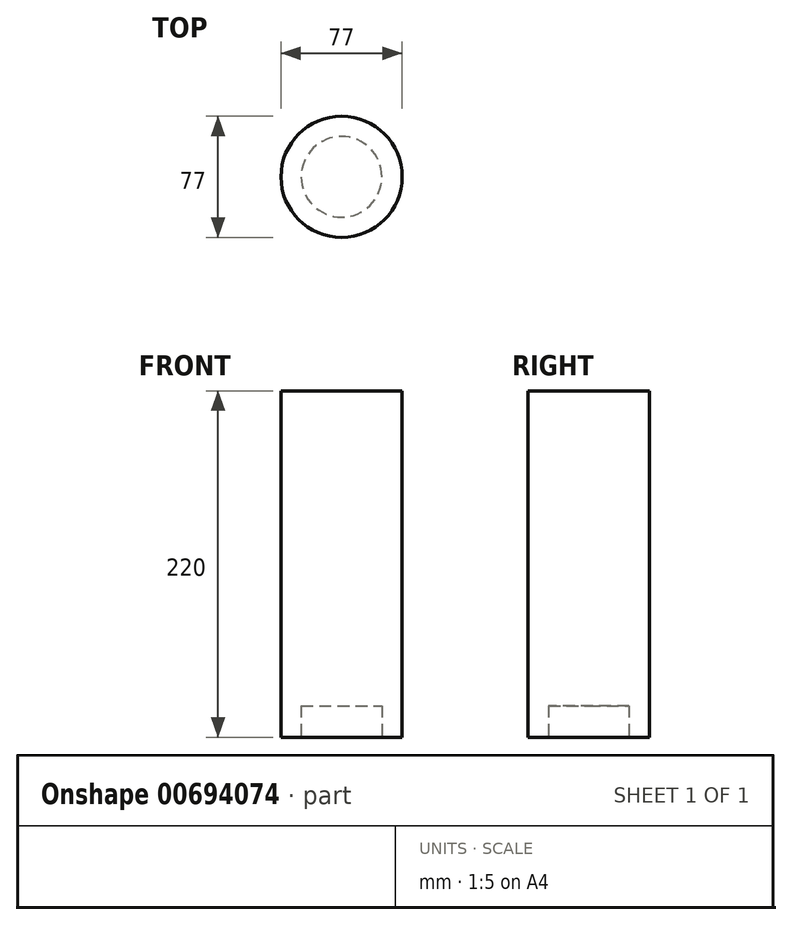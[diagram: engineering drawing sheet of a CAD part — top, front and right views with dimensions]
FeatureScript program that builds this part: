
annotation { "Feature Type Name" : "Feature", "Feature Type Description" : "" }
export const myFeature = defineFeature(function(context is Context, id is Id, definition is map)
    precondition{}
    {
        {
            var Q0;
            Q0=qCreatedBy(makeId("Front.planeOp"),FACE);
            var sketch = newSketch(context, id + "F0", { "sketchPlane" : qUnion([Q0])});
            skLineSegment(sketch, "E0", {"start": v(0, 0) * mm, "end": v(0, 86.33) * mm});
            skLineSegment(sketch, "E1", {"start": v(0, 0) * mm, "end": v(38.5, 0) * mm});
            skLineSegment(sketch, "E2", {"start": v(38.5, 0) * mm, "end": v(38.5, 220) * mm});
            skLineSegment(sketch, "E3", {"start": v(38.5, 220) * mm, "end": v(0, 220) * mm});
            skLineSegment(sketch, "E4", {"start": v(0, 86.33) * mm, "end": v(0, 220) * mm});
            skLineSegment(sketch, "E5.bottom", {"start": v(0, 220) * mm, "end": v(22.5, 220) * mm});
            skLineSegment(sketch, "E5.top", {"start": v(0, 340) * mm, "end": v(22.5, 340) * mm});
            skLineSegment(sketch, "E5.left", {"start": v(0, 220) * mm, "end": v(0, 340) * mm});
            skLineSegment(sketch, "E5.right", {"start": v(22.5, 220) * mm, "end": v(22.5, 340) * mm});
            skLineSegment(sketch, "E6.top", {"start": v(0, 280) * mm, "end": v(22.5, 280) * mm});
            skLineSegment(sketch, "E6.left", {"start": v(0, 220) * mm, "end": v(0, 280) * mm});
            skLineSegment(sketch, "E6.right", {"start": v(22.5, 220) * mm, "end": v(22.5, 280) * mm});
            skLineSegment(sketch, "E7.bottom", {"start": v(0, 280) * mm, "end": v(20.06, 280) * mm});
            skLineSegment(sketch, "E7.top", {"start": v(0, 340) * mm, "end": v(20.06, 340) * mm});
            skLineSegment(sketch, "E7.left", {"start": v(0, 280) * mm, "end": v(0, 340) * mm});
            skLineSegment(sketch, "E7.right", {"start": v(20.06, 280) * mm, "end": v(20.06, 340) * mm});
            skSolve(sketch);
        }
        {
            var Q0;
            Q0=makeQuery(id+"F0.imprint","IMPRINT",FACE,{"disambiguationData":[TD([[makeQuery(id+"F0.imprint","IMPRINT",EDGE,{"derivedFrom":sQuery(id+"F0.wireOp",EDGE,"E5.bottom")}),1.0]])]});
            var Q1;
            Q1=makeQuery(id+"F0.imprint","IMPRINT",FACE,{"disambiguationData":[TD([[makeQuery(id+"F0.imprint","IMPRINT",EDGE,{"derivedFrom":sQuery(id+"F0.wireOp",EDGE,"E5.bottom")}),1.0]])]});
            var Q2;
            Q2=makeQuery(id+"F0.imprint","IMPRINT",FACE,{"disambiguationData":[TD([[makeQuery(id+"F0.imprint","IMPRINT",EDGE,{"derivedFrom":sQuery(id+"F0.wireOp",EDGE,"E7.bottom")}),1.0]])]});
            var Q3;
            Q3=makeQuery(id+"F0.imprint","IMPRINT",FACE,{"disambiguationData":[TD([[makeQuery(id+"F0.imprint","IMPRINT",EDGE,{"derivedFrom":sQuery(id+"F0.wireOp",EDGE,"E0")}),-1.0]])]});
            var Q4;
            Q4=sQuery(id+"F0.wireOp",EDGE,"E0");
            revolve(context, id + "F1", {"entities" : qUnion([Q0, Q1, Q2, Q3]), "axis" : qUnion([Q4]), "revolveType" : RevolveType.FULL});
        }
        {
            var Q0;
            Q0=qCreatedBy(makeId("Front.planeOp"),FACE);
            var sketch = newSketch(context, id + "F2", { "sketchPlane" : qUnion([Q0])});
            skLineSegment(sketch, "E8", {"start": v(0, 0) * mm, "end": v(0, 20.08) * mm});
            skLineSegment(sketch, "E9", {"start": v(0, 20.08) * mm, "end": v(25.62, 20.08) * mm});
            skLineSegment(sketch, "E10", {"start": v(25.62, 20.08) * mm, "end": v(25.62, 0) * mm});
            skLineSegment(sketch, "E11", {"start": v(25.62, 0) * mm, "end": v(0, 0) * mm});
            skSolve(sketch);
        }
        {
            var Q0;
            Q0 = qSketchRegion(id + "F2", true);
            var Q1;
            Q1=sQuery(id+"F2.wireOp",EDGE,"E8");
            revolve(context, id + "F3", {"entities" : qUnion([Q0]), "axis" : qUnion([Q1]), "revolveType" : RevolveType.FULL});
        }
    });
